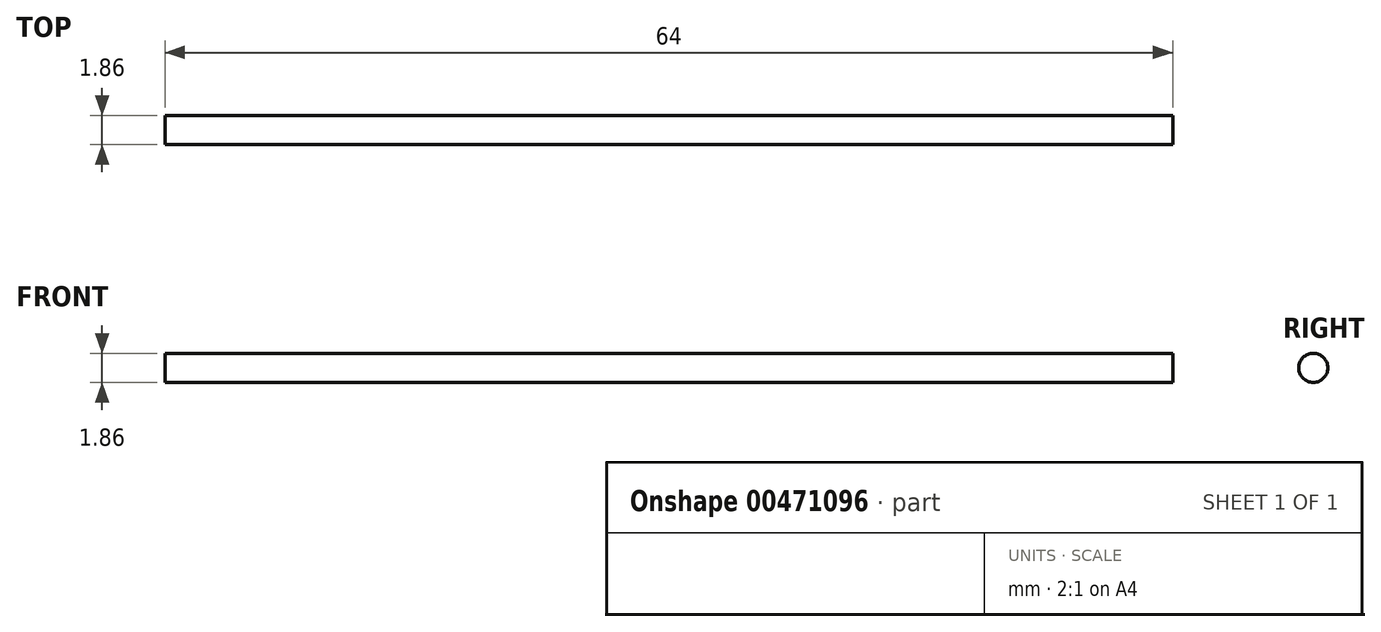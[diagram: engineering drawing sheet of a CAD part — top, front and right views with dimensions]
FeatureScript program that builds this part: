
annotation { "Feature Type Name" : "Feature", "Feature Type Description" : "" }
export const myFeature = defineFeature(function(context is Context, id is Id, definition is map)
    precondition{}
    {
        {
            var Q0;
            Q0=qCreatedBy(makeId("Right.planeOp"),FACE);
            var sketch = newSketch(context, id + "F0", { "sketchPlane" : qUnion([Q0])});
            skCircle(sketch, "E0", {"center": v(0, 0) * mm, "radius": 0.93 * mm});
            skSolve(sketch);
        }
        {
            var Q0;
            Q0 = qSketchRegion(id + "F0", true);
            extrude(context, id + "F1", {"entities" : qUnion([Q0]), "depth" : 64 * mm});
        }
    });
